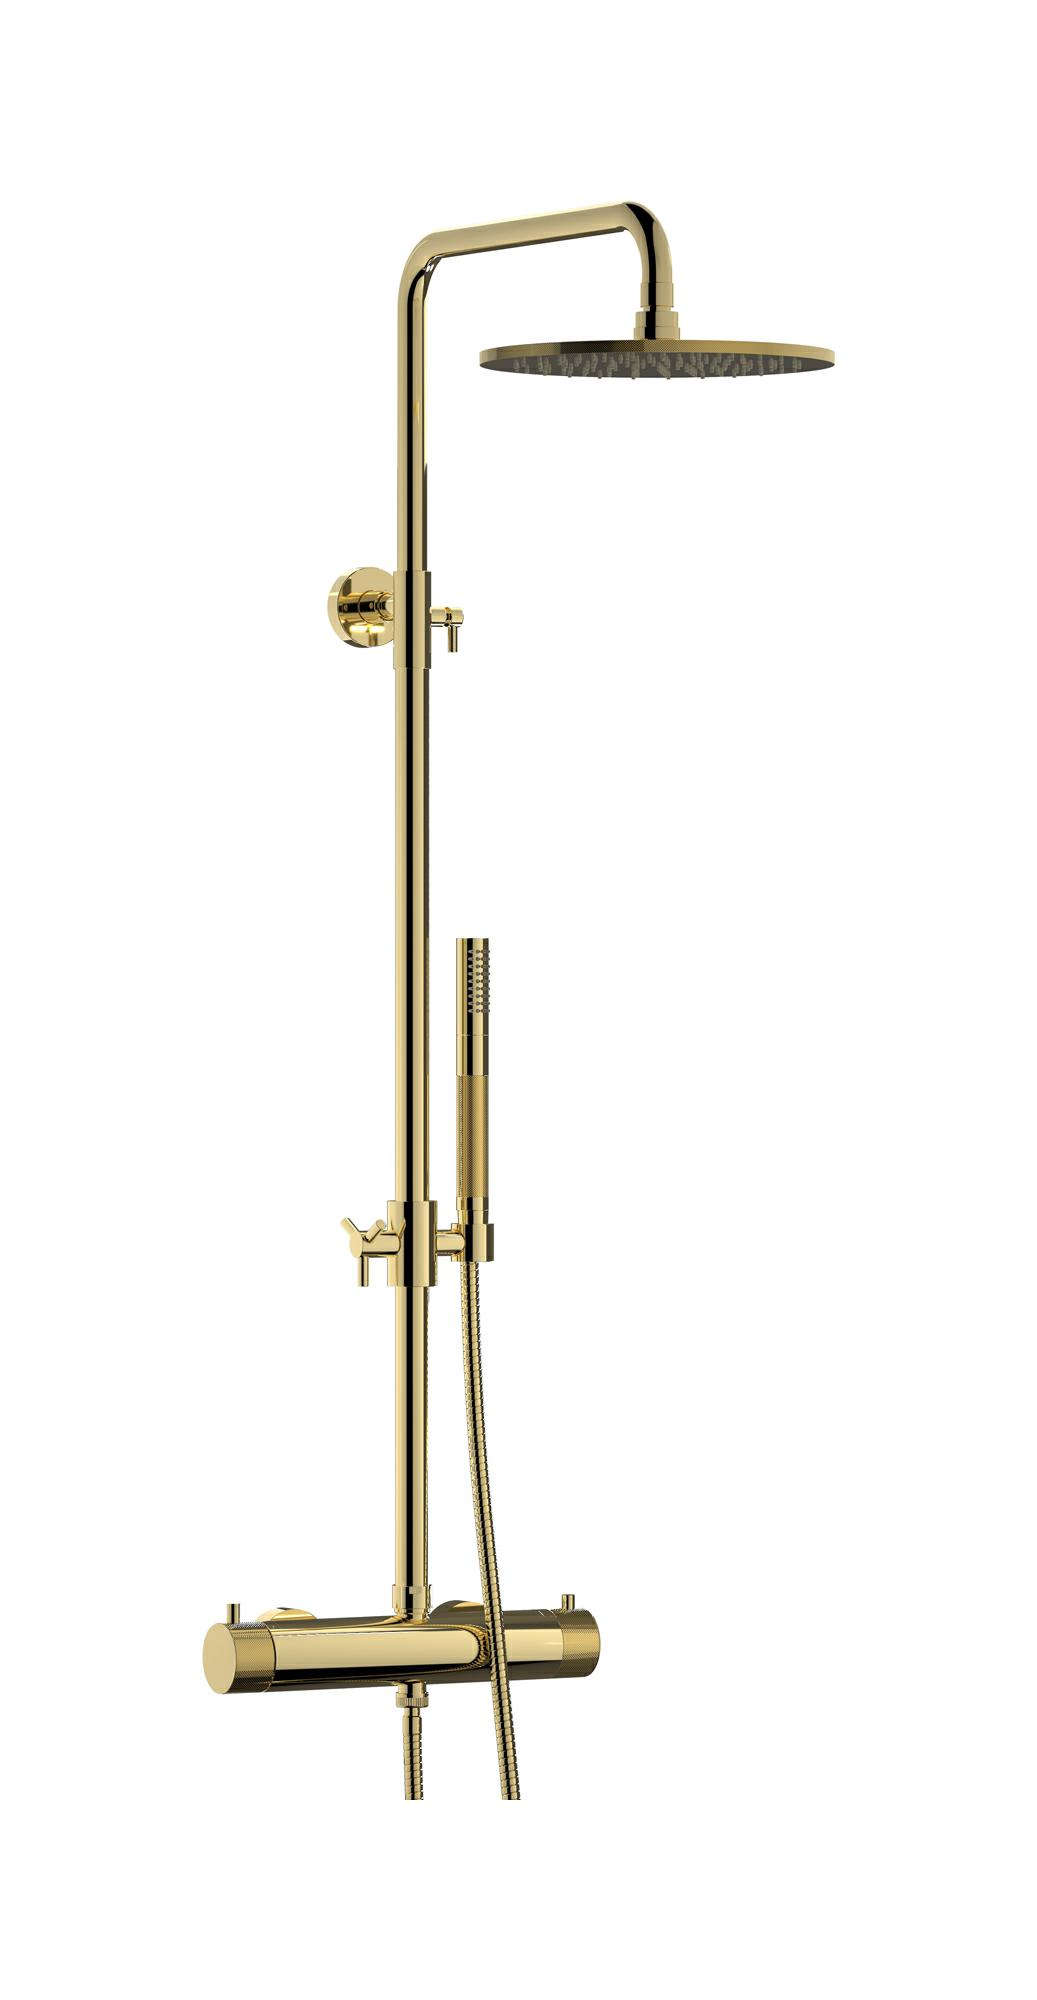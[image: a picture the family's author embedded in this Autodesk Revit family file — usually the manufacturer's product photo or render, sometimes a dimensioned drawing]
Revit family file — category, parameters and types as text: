
# Revit family: ID800
name_source: partatom
category: Apparecchi idraulici
units: mm (PartAtom-declared; Revit-internal decimal feet)

## family parameters
Basato su piano di lavoro = No
Condiviso = No
Mantieni orientamento annotazione = No
Numero OmniClass = 23.45.55.17
Punto di calcolo locali = No
Quota connettore circolare = Usa diametro
Sempre verticale = Sì
Taglio con vuoti quando caricato = No
Tipo di parte = Normale
Titolo OmniClass = Mixing Faucets

## types (12) — shared parameters
Cold water inlet = 10 mm  [stored 0.0328084 ft]
Commenti sul tipo = Shower
Connessione CW = No
Connessione HW = No
Connessione di scarico = No
Connessione di ventilazione = No
Descrizione = Thermostatic shower column with shower kit
Hot water inlet = 10 mm  [stored 0.0328084 ft]
Produttore = IB Rubinetterie S.p.A.
URL = https://www.weareib.it
zero-valued in all types: Prospetto di default

## per-type parameters (varying)
| type | Finishes surface | Immagine tipo | Modello |
| Chrome | IB_Chrome | ID800CC.jpg | ID800CC |
| Brushed nickel | IB_Brushed nickel | ID800SS.jpg | ID800SS |
| Matt black | IB_matt black | ID800NP.jpg | ID800NP |
| Natural brass | IB_Brass | ID800ON.jpg | ID800ON |
| Black chrome | IB_Black chrome | ID800CF.jpg | ID800CF |
| Brushed black chrome | IB_Brushed black chrome | ID800CS.jpg | ID800CS |
| Pale gold | IB_Pale gold | ID800II.jpg | ID800II |
| Brushed pale gold | IB_brushed pale gold | ID800IS.jpg | ID800IS |
| Rose gold | IB_Rose gold | ID800RS.jpg | ID800RS |
| Brushed rose gold | IB_Brushed rose gold | ID800SR.jpg | ID800SR |
| Gold | IB_gold | ID800OO.jpg | ID800OO |
| Brushed gold | IB_brushed gold | ID800OS.jpg | ID800OS |

note: [stored X ft] marks values corroborated as IEEE doubles in the binary element streams (Revit-internal decimal feet)
